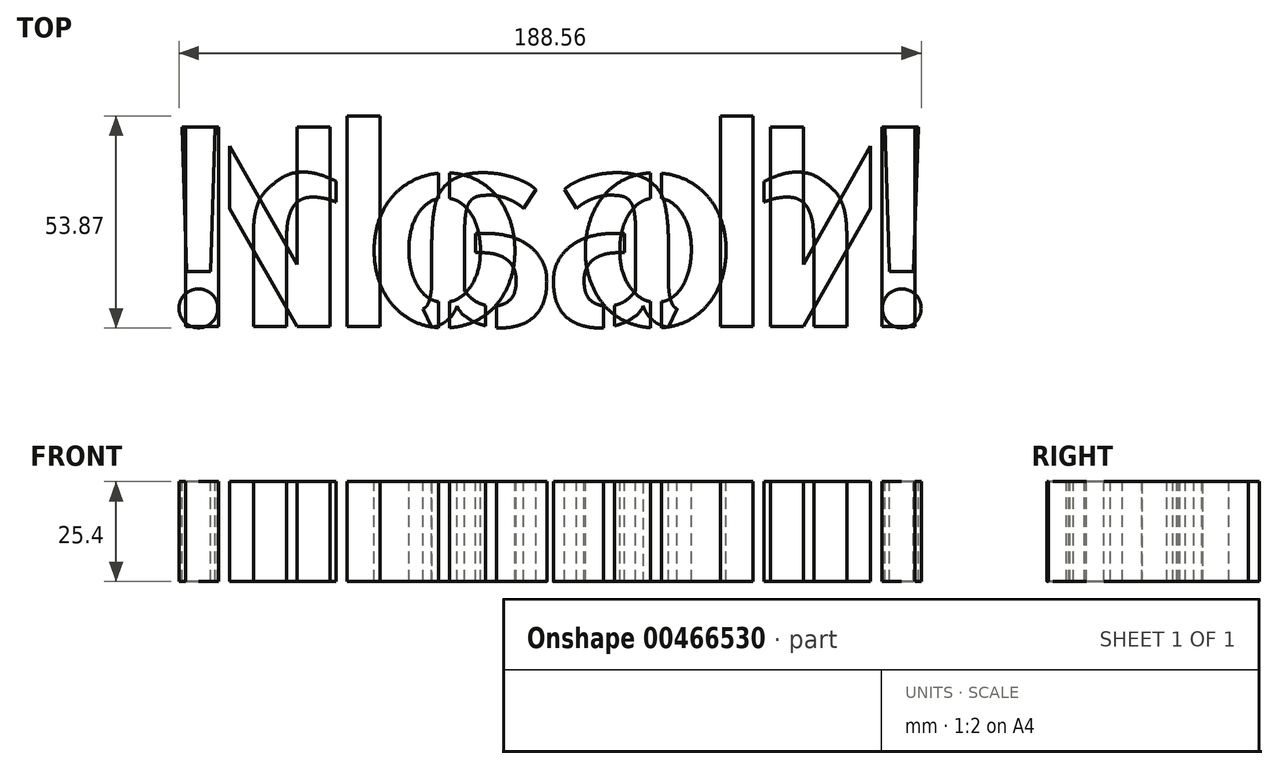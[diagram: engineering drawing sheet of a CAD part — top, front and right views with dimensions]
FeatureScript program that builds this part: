
annotation { "Feature Type Name" : "Feature", "Feature Type Description" : "" }
export const myFeature = defineFeature(function(context is Context, id is Id, definition is map)
    precondition{}
    {
        {
            var Q0;
            Q0=qCreatedBy(makeId("Top.planeOp"),FACE);
            var sketch = newSketch(context, id + "F0", { "sketchPlane" : qUnion([Q0])});
            skLineSegment(sketch, "E0.bottom", {"start": v(99, 25.4) * mm, "end": v(-99, 25.4) * mm, "construction": true});
            skLineSegment(sketch, "E0.top", {"start": v(99, -25.4) * mm, "end": v(-99, -25.4) * mm, "construction": true});
            skLineSegment(sketch, "E0.left", {"start": v(99, 25.4) * mm, "end": v(99, -25.4) * mm, "construction": true});
            skLineSegment(sketch, "E0.right", {"start": v(-99, 25.4) * mm, "end": v(-99, -25.4) * mm, "construction": true});
            skPoint(sketch, "E0.middle", {"position": v(0, 0) * mm});
            skText(sketch, "E1", { "text": "Noah!", "fontName": "AllertaStencil-Regular.ttf"});
            const initialGuessF0  = {"E1": [-0.099, -0.0254, 1, 0, 0.0508]};
            skSetInitialGuess(sketch, initialGuessF0);
            skSolve(sketch);
        }
        {
            var Q0;
            Q0 = qSketchRegion(id + "F0", true);
            extrude(context, id + "F1", {"entities" : qUnion([Q0]), "oppositeDirection" : true, "depth" : 25.4 * mm});
        }
        {
            var Q0;
            Q0=makeQuery(id+"F1.opExtrude","SWEPT_BODY",BODY,{"disambiguationData":[OSD([sQuery(id+"F0.wireOp",EDGE,"E1.sketch_text.stroke-7"),sQuery(id+"F0.wireOp",EDGE,"E1.sketch_text.stroke-8"),sQuery(id+"F0.wireOp",EDGE,"E1.sketch_text.stroke-9"),sQuery(id+"F0.wireOp",EDGE,"E1.sketch_text.stroke-10")])]});
            var Q1;
            Q1=makeQuery(id+"F1.opExtrude","SWEPT_BODY",BODY,{"disambiguationData":[OSD([sQuery(id+"F0.wireOp",EDGE,"E1.sketch_text.stroke-0"),sQuery(id+"F0.wireOp",EDGE,"E1.sketch_text.stroke-1"),sQuery(id+"F0.wireOp",EDGE,"E1.sketch_text.stroke-2"),sQuery(id+"F0.wireOp",EDGE,"E1.sketch_text.stroke-3"),sQuery(id+"F0.wireOp",EDGE,"E1.sketch_text.stroke-4"),sQuery(id+"F0.wireOp",EDGE,"E1.sketch_text.stroke-5"),sQuery(id+"F0.wireOp",EDGE,"E1.sketch_text.stroke-6")])]});
            var Q2;
            Q2=makeQuery(id+"F1.opExtrude","SWEPT_BODY",BODY,{"disambiguationData":[OSD([sQuery(id+"F0.wireOp",EDGE,"E1.sketch_text.stroke-27"),sQuery(id+"F0.wireOp",EDGE,"E1.sketch_text.stroke-28"),sQuery(id+"F0.wireOp",EDGE,"E1.sketch_text.stroke-29"),sQuery(id+"F0.wireOp",EDGE,"E1.sketch_text.stroke-30"),sQuery(id+"F0.wireOp",EDGE,"E1.sketch_text.stroke-31"),sQuery(id+"F0.wireOp",EDGE,"E1.sketch_text.stroke-32"),sQuery(id+"F0.wireOp",EDGE,"E1.sketch_text.stroke-33"),sQuery(id+"F0.wireOp",EDGE,"E1.sketch_text.stroke-34"),sQuery(id+"F0.wireOp",EDGE,"E1.sketch_text.stroke-35"),sQuery(id+"F0.wireOp",EDGE,"E1.sketch_text.stroke-36"),sQuery(id+"F0.wireOp",EDGE,"E1.sketch_text.stroke-37"),sQuery(id+"F0.wireOp",EDGE,"E1.sketch_text.stroke-38"),sQuery(id+"F0.wireOp",EDGE,"E1.sketch_text.stroke-39"),sQuery(id+"F0.wireOp",EDGE,"E1.sketch_text.stroke-40"),sQuery(id+"F0.wireOp",EDGE,"E1.sketch_text.stroke-41"),sQuery(id+"F0.wireOp",EDGE,"E1.sketch_text.stroke-42")])]});
            var Q3;
            Q3=makeQuery(id+"F1.opExtrude","SWEPT_BODY",BODY,{"disambiguationData":[OSD([sQuery(id+"F0.wireOp",EDGE,"E1.sketch_text.stroke-11"),sQuery(id+"F0.wireOp",EDGE,"E1.sketch_text.stroke-12"),sQuery(id+"F0.wireOp",EDGE,"E1.sketch_text.stroke-13"),sQuery(id+"F0.wireOp",EDGE,"E1.sketch_text.stroke-14"),sQuery(id+"F0.wireOp",EDGE,"E1.sketch_text.stroke-15"),sQuery(id+"F0.wireOp",EDGE,"E1.sketch_text.stroke-16"),sQuery(id+"F0.wireOp",EDGE,"E1.sketch_text.stroke-17"),sQuery(id+"F0.wireOp",EDGE,"E1.sketch_text.stroke-18"),sQuery(id+"F0.wireOp",EDGE,"E1.sketch_text.stroke-19"),sQuery(id+"F0.wireOp",EDGE,"E1.sketch_text.stroke-20"),sQuery(id+"F0.wireOp",EDGE,"E1.sketch_text.stroke-21"),sQuery(id+"F0.wireOp",EDGE,"E1.sketch_text.stroke-22"),sQuery(id+"F0.wireOp",EDGE,"E1.sketch_text.stroke-23"),sQuery(id+"F0.wireOp",EDGE,"E1.sketch_text.stroke-24"),sQuery(id+"F0.wireOp",EDGE,"E1.sketch_text.stroke-25"),sQuery(id+"F0.wireOp",EDGE,"E1.sketch_text.stroke-26")])]});
            var Q4;
            Q4=makeQuery(id+"F1.opExtrude","SWEPT_BODY",BODY,{"disambiguationData":[OSD([sQuery(id+"F0.wireOp",EDGE,"E1.sketch_text.stroke-43"),sQuery(id+"F0.wireOp",EDGE,"E1.sketch_text.stroke-44"),sQuery(id+"F0.wireOp",EDGE,"E1.sketch_text.stroke-45"),sQuery(id+"F0.wireOp",EDGE,"E1.sketch_text.stroke-46"),sQuery(id+"F0.wireOp",EDGE,"E1.sketch_text.stroke-47"),sQuery(id+"F0.wireOp",EDGE,"E1.sketch_text.stroke-48"),sQuery(id+"F0.wireOp",EDGE,"E1.sketch_text.stroke-49"),sQuery(id+"F0.wireOp",EDGE,"E1.sketch_text.stroke-50"),sQuery(id+"F0.wireOp",EDGE,"E1.sketch_text.stroke-51"),sQuery(id+"F0.wireOp",EDGE,"E1.sketch_text.stroke-52"),sQuery(id+"F0.wireOp",EDGE,"E1.sketch_text.stroke-53"),sQuery(id+"F0.wireOp",EDGE,"E1.sketch_text.stroke-54"),sQuery(id+"F0.wireOp",EDGE,"E1.sketch_text.stroke-55"),sQuery(id+"F0.wireOp",EDGE,"E1.sketch_text.stroke-56"),sQuery(id+"F0.wireOp",EDGE,"E1.sketch_text.stroke-57"),sQuery(id+"F0.wireOp",EDGE,"E1.sketch_text.stroke-58"),sQuery(id+"F0.wireOp",EDGE,"E1.sketch_text.stroke-59"),sQuery(id+"F0.wireOp",EDGE,"E1.sketch_text.stroke-60"),sQuery(id+"F0.wireOp",EDGE,"E1.sketch_text.stroke-61")])]});
            var Q5;
            Q5=makeQuery(id+"F1.opExtrude","SWEPT_BODY",BODY,{"disambiguationData":[OSD([sQuery(id+"F0.wireOp",EDGE,"E1.sketch_text.stroke-62"),sQuery(id+"F0.wireOp",EDGE,"E1.sketch_text.stroke-63"),sQuery(id+"F0.wireOp",EDGE,"E1.sketch_text.stroke-64"),sQuery(id+"F0.wireOp",EDGE,"E1.sketch_text.stroke-65"),sQuery(id+"F0.wireOp",EDGE,"E1.sketch_text.stroke-66"),sQuery(id+"F0.wireOp",EDGE,"E1.sketch_text.stroke-67"),sQuery(id+"F0.wireOp",EDGE,"E1.sketch_text.stroke-68"),sQuery(id+"F0.wireOp",EDGE,"E1.sketch_text.stroke-69"),sQuery(id+"F0.wireOp",EDGE,"E1.sketch_text.stroke-70"),sQuery(id+"F0.wireOp",EDGE,"E1.sketch_text.stroke-71"),sQuery(id+"F0.wireOp",EDGE,"E1.sketch_text.stroke-72"),sQuery(id+"F0.wireOp",EDGE,"E1.sketch_text.stroke-73"),sQuery(id+"F0.wireOp",EDGE,"E1.sketch_text.stroke-74"),sQuery(id+"F0.wireOp",EDGE,"E1.sketch_text.stroke-75"),sQuery(id+"F0.wireOp",EDGE,"E1.sketch_text.stroke-76"),sQuery(id+"F0.wireOp",EDGE,"E1.sketch_text.stroke-77"),sQuery(id+"F0.wireOp",EDGE,"E1.sketch_text.stroke-78"),sQuery(id+"F0.wireOp",EDGE,"E1.sketch_text.stroke-79"),sQuery(id+"F0.wireOp",EDGE,"E1.sketch_text.stroke-80"),sQuery(id+"F0.wireOp",EDGE,"E1.sketch_text.stroke-81"),sQuery(id+"F0.wireOp",EDGE,"E1.sketch_text.stroke-82"),sQuery(id+"F0.wireOp",EDGE,"E1.sketch_text.stroke-83"),sQuery(id+"F0.wireOp",EDGE,"E1.sketch_text.stroke-84"),sQuery(id+"F0.wireOp",EDGE,"E1.sketch_text.stroke-85"),sQuery(id+"F0.wireOp",EDGE,"E1.sketch_text.stroke-86"),sQuery(id+"F0.wireOp",EDGE,"E1.sketch_text.stroke-87"),sQuery(id+"F0.wireOp",EDGE,"E1.sketch_text.stroke-88"),sQuery(id+"F0.wireOp",EDGE,"E1.sketch_text.stroke-89"),sQuery(id+"F0.wireOp",EDGE,"E1.sketch_text.stroke-90"),sQuery(id+"F0.wireOp",EDGE,"E1.sketch_text.stroke-91"),sQuery(id+"F0.wireOp",EDGE,"E1.sketch_text.stroke-92"),sQuery(id+"F0.wireOp",EDGE,"E1.sketch_text.stroke-93"),sQuery(id+"F0.wireOp",EDGE,"E1.sketch_text.stroke-94"),sQuery(id+"F0.wireOp",EDGE,"E1.sketch_text.stroke-95"),sQuery(id+"F0.wireOp",EDGE,"E1.sketch_text.stroke-96"),sQuery(id+"F0.wireOp",EDGE,"E1.sketch_text.stroke-97")])]});
            var Q6;
            Q6=makeQuery(id+"F1.opExtrude","SWEPT_BODY",BODY,{"disambiguationData":[OSD([sQuery(id+"F0.wireOp",EDGE,"E1.sketch_text.stroke-98"),sQuery(id+"F0.wireOp",EDGE,"E1.sketch_text.stroke-99"),sQuery(id+"F0.wireOp",EDGE,"E1.sketch_text.stroke-100"),sQuery(id+"F0.wireOp",EDGE,"E1.sketch_text.stroke-101")])]});
            var Q7;
            Q7=makeQuery(id+"F1.opExtrude","SWEPT_BODY",BODY,{"disambiguationData":[OSD([sQuery(id+"F0.wireOp",EDGE,"E1.sketch_text.stroke-102"),sQuery(id+"F0.wireOp",EDGE,"E1.sketch_text.stroke-103"),sQuery(id+"F0.wireOp",EDGE,"E1.sketch_text.stroke-104"),sQuery(id+"F0.wireOp",EDGE,"E1.sketch_text.stroke-105"),sQuery(id+"F0.wireOp",EDGE,"E1.sketch_text.stroke-106"),sQuery(id+"F0.wireOp",EDGE,"E1.sketch_text.stroke-107"),sQuery(id+"F0.wireOp",EDGE,"E1.sketch_text.stroke-108"),sQuery(id+"F0.wireOp",EDGE,"E1.sketch_text.stroke-109"),sQuery(id+"F0.wireOp",EDGE,"E1.sketch_text.stroke-110"),sQuery(id+"F0.wireOp",EDGE,"E1.sketch_text.stroke-111"),sQuery(id+"F0.wireOp",EDGE,"E1.sketch_text.stroke-112"),sQuery(id+"F0.wireOp",EDGE,"E1.sketch_text.stroke-113"),sQuery(id+"F0.wireOp",EDGE,"E1.sketch_text.stroke-114"),sQuery(id+"F0.wireOp",EDGE,"E1.sketch_text.stroke-115"),sQuery(id+"F0.wireOp",EDGE,"E1.sketch_text.stroke-116"),sQuery(id+"F0.wireOp",EDGE,"E1.sketch_text.stroke-117"),sQuery(id+"F0.wireOp",EDGE,"E1.sketch_text.stroke-118"),sQuery(id+"F0.wireOp",EDGE,"E1.sketch_text.stroke-119"),sQuery(id+"F0.wireOp",EDGE,"E1.sketch_text.stroke-120")])]});
            var Q8;
            Q8=makeQuery(id+"F1.opExtrude","SWEPT_BODY",BODY,{"disambiguationData":[OSD([sQuery(id+"F0.wireOp",EDGE,"E1.sketch_text.stroke-121"),sQuery(id+"F0.wireOp",EDGE,"E1.sketch_text.stroke-122"),sQuery(id+"F0.wireOp",EDGE,"E1.sketch_text.stroke-123"),sQuery(id+"F0.wireOp",EDGE,"E1.sketch_text.stroke-124")])]});
            var Q9;
            Q9=makeQuery(id+"F1.opExtrude","SWEPT_BODY",BODY,{"disambiguationData":[OSD([sQuery(id+"F0.wireOp",EDGE,"E1.sketch_text.stroke-125"),sQuery(id+"F0.wireOp",EDGE,"E1.sketch_text.stroke-126"),sQuery(id+"F0.wireOp",EDGE,"E1.sketch_text.stroke-127"),sQuery(id+"F0.wireOp",EDGE,"E1.sketch_text.stroke-128"),sQuery(id+"F0.wireOp",EDGE,"E1.sketch_text.stroke-129"),sQuery(id+"F0.wireOp",EDGE,"E1.sketch_text.stroke-130"),sQuery(id+"F0.wireOp",EDGE,"E1.sketch_text.stroke-131"),sQuery(id+"F0.wireOp",EDGE,"E1.sketch_text.stroke-132")])]});
            var Q10;
            Q10=qCreatedBy(makeId("Right.planeOp"),FACE);
            mirror(context, id + "F2", {"entities" : qUnion([Q0, Q1, Q2, Q3, Q4, Q5, Q6, Q7, Q8, Q9]), "mirrorPlane" : qUnion([Q10])});
        }
    });
